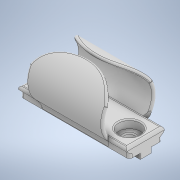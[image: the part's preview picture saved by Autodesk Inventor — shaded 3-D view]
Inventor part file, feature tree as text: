
AUTODESK INVENTOR PART (.ipt)
format: ipt  version: 2020 (Build 240168000, 168)  size: 463,872 bytes
history: native  units: in
note: dims shown in document units (in); Inventor stores cm internally (conversion verified against a paired STEP export)
features: fillet x7, sketch x6, extrude x4, hole x1, emboss x1
ambient origin geometry x8: Origin, YZ Plane, XZ Plane, XY Plane, X Axis, Y Axis, Z Axis, Center Point
bodies: Solid1 (feature_tree)
feature tree (19):
  extrude  "Extrusion1"  Depth=0.6in
  extrude  "Extrusion2"  Depth=0.3in
  sketch  "Sketch3"  dims[d5=0.88in d6=1.0in]
  extrude  "Extrusion3"  Depth=1.0in
  hole  "Hole1"  [1 undecoded]
  extrude  "Extrusion4"  Depth=0.3in
  fillet  "Fillet1"  Radius=0.3in
  fillet  "Fillet2"  Radius=0.1in
  fillet  "Fillet3"  Radius=2.0in
  fillet  "Fillet4"  Radius=0.2in
  fillet  "Fillet5"  Radius=0.1in
  fillet  "Fillet6"  Radius=0.5in
  emboss  "Emboss1"
  fillet  "Fillet7"  Radius=1.0in
  sketch  "Sketch1"  dims[d0=2.0in d1=0.6in]
  sketch  "Sketch2"  dims[d2=0.2in d3=0.0in d4=0.3in]
  sketch  "Sketch4"  dims[d7=0.06in d8=0.12in]
  sketch  "Sketch6"  dims[d9=2.0in d10=0.0in d11=0.3in d12=0.3in d13=0.1in d14=2.0in d15=0.2in d16=0.1in d17=0.0in]
  sketch  "Sketch7"  dims[d18=0.2in d19=0.75in d20=0.4in d21=0.15in d22=0.5635in d23=1.0in d24=0.8108in d35=0.5in d36=1.0in d37=0.3in d38=0.5in d39=1.0in d40=0.3in d41=0.1in d42=0.1in d43=0.06in d44=0.12in d45=1.0in d46=0.0in d47=0.125in d48=0.05in d49=0.2in d50=0.03in d51=0.02in d52=0.03in d53=0.05in d54=0.0in d55=0.05in]
note: 1 required parameter value undecoded (feature->parameter linkage not recoverable at this tier; creation-order binding heuristic only, values carry confidence <= 0.55)
